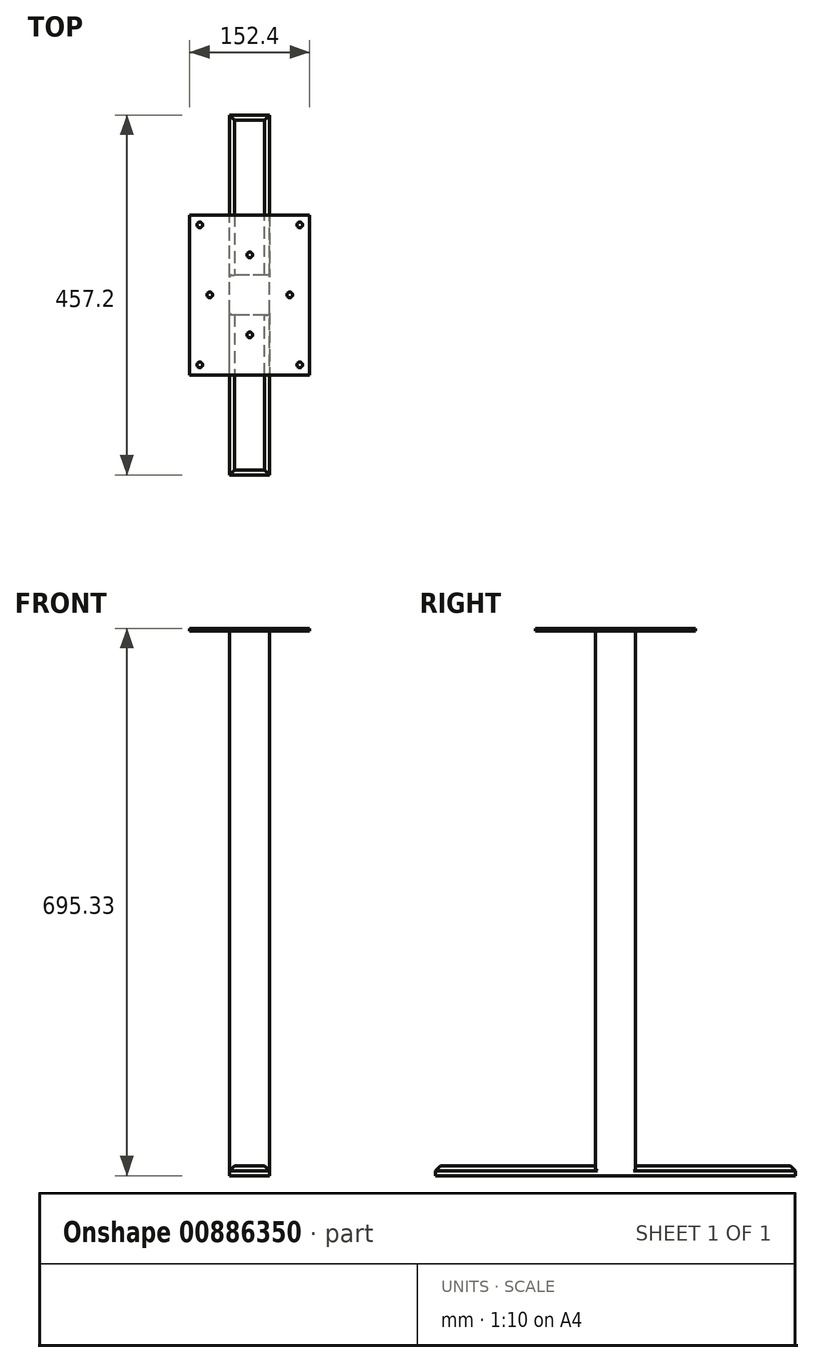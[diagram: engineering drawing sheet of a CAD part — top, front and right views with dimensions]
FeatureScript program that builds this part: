
annotation { "Feature Type Name" : "Feature", "Feature Type Description" : "" }
export const myFeature = defineFeature(function(context is Context, id is Id, definition is map)
    precondition{}
    {
        {
            var Q0;
            Q0=qCreatedBy(makeId("Top.planeOp"),FACE);
            var sketch = newSketch(context, id + "F0", { "sketchPlane" : qUnion([Q0])});
            skLineSegment(sketch, "E0.bottom", {"start": v(76.2, 101.6) * mm, "end": v(-76.2, 101.6) * mm});
            skLineSegment(sketch, "E0.top", {"start": v(76.2, -101.6) * mm, "end": v(-76.2, -101.6) * mm});
            skLineSegment(sketch, "E0.left", {"start": v(76.2, 101.6) * mm, "end": v(76.2, -101.6) * mm});
            skLineSegment(sketch, "E0.right", {"start": v(-76.2, 101.6) * mm, "end": v(-76.2, -101.6) * mm});
            skPoint(sketch, "E0.middle", {"position": v(0, 0) * mm});
            skSolve(sketch);
        }
        {
            var Q0;
            Q0 = qSketchRegion(id + "F0", true);
            extrude(context, id + "F1", {"entities" : qUnion([Q0]), "depth" : 3.17 * mm, "offsetDistance" : 25.4 * mm});
        }
        {
            var Q0;
            Q0=makeQuery(id+"F1.opExtrude","CAP_FACE",FACE,{"disambiguationData":[OSD([sQuery(id+"F0.wireOp",EDGE,"E0.bottom"),sQuery(id+"F0.wireOp",EDGE,"E0.top"),sQuery(id+"F0.wireOp",EDGE,"E0.left"),sQuery(id+"F0.wireOp",EDGE,"E0.right")])],"isStart":false});
            var sketch = newSketch(context, id + "F2", { "sketchPlane" : qUnion([Q0])});
            skLineSegment(sketch, "E1.bottom", {"start": v(63.5, 88.9) * mm, "end": v(-63.5, 88.9) * mm});
            skLineSegment(sketch, "E1.top", {"start": v(63.5, -88.9) * mm, "end": v(-63.5, -88.9) * mm});
            skLineSegment(sketch, "E1.left", {"start": v(63.5, 88.9) * mm, "end": v(63.5, -88.9) * mm});
            skLineSegment(sketch, "E1.right", {"start": v(-63.5, 88.9) * mm, "end": v(-63.5, -88.9) * mm});
            skPoint(sketch, "E1.middle", {"position": v(0, 0) * mm});
            skCircle(sketch, "E2", {"center": v(-63.5, 88.9) * mm, "radius": 3.57 * mm});
            skCircle(sketch, "E3", {"center": v(63.5, 88.9) * mm, "radius": 3.57 * mm});
            skCircle(sketch, "E4", {"center": v(63.5, -88.9) * mm, "radius": 3.57 * mm});
            skCircle(sketch, "E5", {"center": v(-63.5, -88.9) * mm, "radius": 3.57 * mm});
            skLineSegment(sketch, "E6.0", {"start": v(0, 50.8) * mm, "end": v(50.8, 0) * mm});
            skLineSegment(sketch, "E6.1", {"start": v(50.8, 0) * mm, "end": v(0, -50.8) * mm});
            skLineSegment(sketch, "E6.2", {"start": v(0, -50.8) * mm, "end": v(-50.8, 0) * mm});
            skLineSegment(sketch, "E6.3", {"start": v(-50.8, 0) * mm, "end": v(0, 50.8) * mm});
            skPoint(sketch, "E7", {"position": v(0, 50.8) * mm});
            skCircle(sketch, "E8", {"center": v(0, 50.8) * mm, "radius": 3.57 * mm});
            skCircle(sketch, "E9", {"center": v(-50.8, 0) * mm, "radius": 3.57 * mm});
            skCircle(sketch, "E10", {"center": v(50.8, 0) * mm, "radius": 3.57 * mm});
            skCircle(sketch, "E11", {"center": v(0, -50.8) * mm, "radius": 3.57 * mm});
            skSolve(sketch);
        }
        {
            var Q0;
            {var subQ0=sQuery(id+"F2.wireOp",EDGE,"E6.3");var subQ1=sQuery(id+"F2.wireOp",EDGE,"E6.0");var subQ2=makeQuery(id+"F2.imprint","INTERSECT",VERTEX,{"derivedFrom":[subQ1,subQ0]});Q0=makeQuery(id+"F2.imprint","IMPRINT",FACE,{"disambiguationData":[TD([[makeQuery(id+"F2.imprint","IMPRINT",EDGE,{"disambiguationData":[TD([[subQ2,-1.0]])],"derivedFrom":subQ1}),1.0]])]});}
            var Q1;
            {var subQ0=sQuery(id+"F2.wireOp",EDGE,"E6.3");var subQ1=sQuery(id+"F2.wireOp",EDGE,"E6.0");var subQ2=makeQuery(id+"F2.imprint","INTERSECT",VERTEX,{"derivedFrom":[subQ1,subQ0]});Q1=makeQuery(id+"F2.imprint","IMPRINT",FACE,{"disambiguationData":[TD([[makeQuery(id+"F2.imprint","IMPRINT",EDGE,{"disambiguationData":[TD([[subQ2,-1.0]])],"derivedFrom":subQ1}),-1.0]])]});}
            var Q2;
            {var subQ0=sQuery(id+"F2.wireOp",EDGE,"E6.3");var subQ1=sQuery(id+"F2.wireOp",EDGE,"E6.2");var subQ2=makeQuery(id+"F2.imprint","INTERSECT",VERTEX,{"derivedFrom":[subQ1,subQ0]});Q2=makeQuery(id+"F2.imprint","IMPRINT",FACE,{"disambiguationData":[TD([[makeQuery(id+"F2.imprint","IMPRINT",EDGE,{"disambiguationData":[TD([[subQ2,1.0]])],"derivedFrom":subQ1}),1.0]])]});}
            var Q3;
            {var subQ0=sQuery(id+"F2.wireOp",EDGE,"E6.3");var subQ1=sQuery(id+"F2.wireOp",EDGE,"E6.2");var subQ2=makeQuery(id+"F2.imprint","INTERSECT",VERTEX,{"derivedFrom":[subQ1,subQ0]});Q3=makeQuery(id+"F2.imprint","IMPRINT",FACE,{"disambiguationData":[TD([[makeQuery(id+"F2.imprint","IMPRINT",EDGE,{"disambiguationData":[TD([[subQ2,1.0]])],"derivedFrom":subQ1}),-1.0]])]});}
            var Q4;
            {var subQ0=sQuery(id+"F2.wireOp",EDGE,"E6.1");var subQ1=sQuery(id+"F2.wireOp",EDGE,"E6.0");var subQ2=makeQuery(id+"F2.imprint","INTERSECT",VERTEX,{"derivedFrom":[subQ1,subQ0]});Q4=makeQuery(id+"F2.imprint","IMPRINT",FACE,{"disambiguationData":[TD([[makeQuery(id+"F2.imprint","IMPRINT",EDGE,{"disambiguationData":[TD([[subQ2,1.0]])],"derivedFrom":subQ1}),-1.0]])]});}
            var Q5;
            {var subQ0=sQuery(id+"F2.wireOp",EDGE,"E6.1");var subQ1=sQuery(id+"F2.wireOp",EDGE,"E6.0");var subQ2=makeQuery(id+"F2.imprint","INTERSECT",VERTEX,{"derivedFrom":[subQ1,subQ0]});Q5=makeQuery(id+"F2.imprint","IMPRINT",FACE,{"disambiguationData":[TD([[makeQuery(id+"F2.imprint","IMPRINT",EDGE,{"disambiguationData":[TD([[subQ2,1.0]])],"derivedFrom":subQ1}),1.0]])]});}
            var Q6;
            {var subQ0=sQuery(id+"F2.wireOp",EDGE,"E6.2");var subQ1=sQuery(id+"F2.wireOp",EDGE,"E6.1");var subQ2=makeQuery(id+"F2.imprint","INTERSECT",VERTEX,{"derivedFrom":[subQ1,subQ0]});Q6=makeQuery(id+"F2.imprint","IMPRINT",FACE,{"disambiguationData":[TD([[makeQuery(id+"F2.imprint","IMPRINT",EDGE,{"disambiguationData":[TD([[subQ2,1.0]])],"derivedFrom":subQ1}),-1.0]])]});}
            var Q7;
            {var subQ0=sQuery(id+"F2.wireOp",EDGE,"E6.2");var subQ1=sQuery(id+"F2.wireOp",EDGE,"E6.1");var subQ2=makeQuery(id+"F2.imprint","INTERSECT",VERTEX,{"derivedFrom":[subQ1,subQ0]});Q7=makeQuery(id+"F2.imprint","IMPRINT",FACE,{"disambiguationData":[TD([[makeQuery(id+"F2.imprint","IMPRINT",EDGE,{"disambiguationData":[TD([[subQ2,1.0]])],"derivedFrom":subQ1}),1.0]])]});}
            var Q8;
            {var subQ0=sQuery(id+"F2.wireOp",EDGE,"E1.right");var subQ1=sQuery(id+"F2.wireOp",EDGE,"E1.top");var subQ2=makeQuery(id+"F2.imprint","INTERSECT",VERTEX,{"derivedFrom":[subQ1,subQ0]});Q8=makeQuery(id+"F2.imprint","IMPRINT",FACE,{"disambiguationData":[TD([[makeQuery(id+"F2.imprint","IMPRINT",EDGE,{"disambiguationData":[TD([[subQ2,1.0]])],"derivedFrom":subQ1}),-1.0]])]});}
            var Q9;
            {var subQ0=sQuery(id+"F2.wireOp",EDGE,"E1.right");var subQ1=sQuery(id+"F2.wireOp",EDGE,"E1.top");var subQ2=makeQuery(id+"F2.imprint","INTERSECT",VERTEX,{"derivedFrom":[subQ1,subQ0]});Q9=makeQuery(id+"F2.imprint","IMPRINT",FACE,{"disambiguationData":[TD([[makeQuery(id+"F2.imprint","IMPRINT",EDGE,{"disambiguationData":[TD([[subQ2,1.0]])],"derivedFrom":subQ1}),1.0]])]});}
            var Q10;
            {var subQ0=sQuery(id+"F2.wireOp",EDGE,"E1.left");var subQ1=sQuery(id+"F2.wireOp",EDGE,"E1.top");var subQ2=makeQuery(id+"F2.imprint","INTERSECT",VERTEX,{"derivedFrom":[subQ1,subQ0]});Q10=makeQuery(id+"F2.imprint","IMPRINT",FACE,{"disambiguationData":[TD([[makeQuery(id+"F2.imprint","IMPRINT",EDGE,{"disambiguationData":[TD([[subQ2,-1.0]])],"derivedFrom":subQ1}),-1.0]])]});}
            var Q11;
            {var subQ0=sQuery(id+"F2.wireOp",EDGE,"E1.left");var subQ1=sQuery(id+"F2.wireOp",EDGE,"E1.top");var subQ2=makeQuery(id+"F2.imprint","INTERSECT",VERTEX,{"derivedFrom":[subQ1,subQ0]});Q11=makeQuery(id+"F2.imprint","IMPRINT",FACE,{"disambiguationData":[TD([[makeQuery(id+"F2.imprint","IMPRINT",EDGE,{"disambiguationData":[TD([[subQ2,-1.0]])],"derivedFrom":subQ1}),1.0]])]});}
            var Q12;
            {var subQ0=sQuery(id+"F2.wireOp",EDGE,"E1.left");var subQ1=sQuery(id+"F2.wireOp",EDGE,"E1.bottom");var subQ2=makeQuery(id+"F2.imprint","INTERSECT",VERTEX,{"derivedFrom":[subQ1,subQ0]});Q12=makeQuery(id+"F2.imprint","IMPRINT",FACE,{"disambiguationData":[TD([[makeQuery(id+"F2.imprint","IMPRINT",EDGE,{"disambiguationData":[TD([[subQ2,-1.0]])],"derivedFrom":subQ1}),-1.0]])]});}
            var Q13;
            {var subQ0=sQuery(id+"F2.wireOp",EDGE,"E1.left");var subQ1=sQuery(id+"F2.wireOp",EDGE,"E1.bottom");var subQ2=makeQuery(id+"F2.imprint","INTERSECT",VERTEX,{"derivedFrom":[subQ1,subQ0]});Q13=makeQuery(id+"F2.imprint","IMPRINT",FACE,{"disambiguationData":[TD([[makeQuery(id+"F2.imprint","IMPRINT",EDGE,{"disambiguationData":[TD([[subQ2,-1.0]])],"derivedFrom":subQ1}),1.0]])]});}
            var Q14;
            {var subQ0=sQuery(id+"F2.wireOp",EDGE,"E1.right");var subQ1=sQuery(id+"F2.wireOp",EDGE,"E1.bottom");var subQ2=makeQuery(id+"F2.imprint","INTERSECT",VERTEX,{"derivedFrom":[subQ1,subQ0]});Q14=makeQuery(id+"F2.imprint","IMPRINT",FACE,{"disambiguationData":[TD([[makeQuery(id+"F2.imprint","IMPRINT",EDGE,{"disambiguationData":[TD([[subQ2,1.0]])],"derivedFrom":subQ1}),-1.0]])]});}
            var Q15;
            {var subQ0=sQuery(id+"F2.wireOp",EDGE,"E1.right");var subQ1=sQuery(id+"F2.wireOp",EDGE,"E1.bottom");var subQ2=makeQuery(id+"F2.imprint","INTERSECT",VERTEX,{"derivedFrom":[subQ1,subQ0]});Q15=makeQuery(id+"F2.imprint","IMPRINT",FACE,{"disambiguationData":[TD([[makeQuery(id+"F2.imprint","IMPRINT",EDGE,{"disambiguationData":[TD([[subQ2,1.0]])],"derivedFrom":subQ1}),1.0]])]});}
            extrude(context, id + "F3", {"entities" : qUnion([Q0, Q1, Q2, Q3, Q4, Q5, Q6, Q7, Q8, Q9, Q10, Q11, Q12, Q13, Q14, Q15]), "operationType" : NewBodyOperationType.REMOVE, "oppositeDirection" : true, "depth" : 25.4 * mm, "offsetDistance" : 25.4 * mm});
        }
        {
            var Q0;
            Q0=makeQuery(id+"F1.opExtrude","CAP_FACE",FACE,{"disambiguationData":[OSD([sQuery(id+"F0.wireOp",EDGE,"E0.bottom"),sQuery(id+"F0.wireOp",EDGE,"E0.top"),sQuery(id+"F0.wireOp",EDGE,"E0.left"),sQuery(id+"F0.wireOp",EDGE,"E0.right")])],"isStart":true});
            var sketch = newSketch(context, id + "F4", { "sketchPlane" : qUnion([Q0])});
            skLineSegment(sketch, "E12.bottom", {"start": v(25.4, 25.4) * mm, "end": v(-25.4, 25.4) * mm});
            skLineSegment(sketch, "E12.top", {"start": v(25.4, -25.4) * mm, "end": v(-25.4, -25.4) * mm});
            skLineSegment(sketch, "E12.left", {"start": v(25.4, 25.4) * mm, "end": v(25.4, -25.4) * mm});
            skLineSegment(sketch, "E12.right", {"start": v(-25.4, 25.4) * mm, "end": v(-25.4, -25.4) * mm});
            skPoint(sketch, "E12.middle", {"position": v(0, 0) * mm});
            skSolve(sketch);
        }
        {
            var Q0;
            Q0=makeQuery(id+"F4.imprint","IMPRINT",FACE,{"disambiguationData":[TD([[makeQuery(id+"F4.imprint","IMPRINT",EDGE,{"derivedFrom":sQuery(id+"F4.wireOp",EDGE,"E12.bottom")}),1.0]])]});
            extrude(context, id + "F5", {"entities" : qUnion([Q0]), "operationType" : NewBodyOperationType.ADD, "depth" : 679.45 * mm, "offsetDistance" : 25.4 * mm});
        }
        {
            var Q0;
            Q0=makeQuery(id+"F5.opExtrude","SWEPT_EDGE",EDGE,{"disambiguationData":[OSD([sQuery(id+"F4.wireOp",EDGE,"E12.bottom"),sQuery(id+"F4.wireOp",EDGE,"E12.right")])]});
            var Q1;
            Q1=makeQuery(id+"F5.opExtrude","SWEPT_EDGE",EDGE,{"disambiguationData":[OSD([sQuery(id+"F4.wireOp",EDGE,"E12.bottom"),sQuery(id+"F4.wireOp",EDGE,"E12.left")])]});
            var Q2;
            Q2=makeQuery(id+"F5.opExtrude","SWEPT_EDGE",EDGE,{"disambiguationData":[OSD([sQuery(id+"F4.wireOp",EDGE,"E12.top"),sQuery(id+"F4.wireOp",EDGE,"E12.left")])]});
            var Q3;
            Q3=makeQuery(id+"F5.opExtrude","SWEPT_EDGE",EDGE,{"disambiguationData":[OSD([sQuery(id+"F4.wireOp",EDGE,"E12.top"),sQuery(id+"F4.wireOp",EDGE,"E12.right")])]});
            fillet(context, id + "F6", {"entities" : qUnion([Q0, Q1, Q2, Q3]), "radius" : 2.54 * mm, "tangentPropagation" : true, "allowEdgeOverflow" : false});
        }
        {
            var Q0;
            Q0=makeQuery(id+"F5.opExtrude","CAP_FACE",FACE,{"disambiguationData":[OSD([sQuery(id+"F4.wireOp",EDGE,"E12.bottom"),sQuery(id+"F4.wireOp",EDGE,"E12.top"),sQuery(id+"F4.wireOp",EDGE,"E12.left"),sQuery(id+"F4.wireOp",EDGE,"E12.right")])],"isStart":false});
            var sketch = newSketch(context, id + "F7", { "sketchPlane" : qUnion([Q0])});
            skLineSegment(sketch, "E13.bottom", {"start": v(25.4, 228.6) * mm, "end": v(-25.4, 228.6) * mm});
            skLineSegment(sketch, "E13.top", {"start": v(25.4, -228.6) * mm, "end": v(-25.4, -228.6) * mm});
            skLineSegment(sketch, "E13.left", {"start": v(25.4, 228.6) * mm, "end": v(25.4, -228.6) * mm});
            skLineSegment(sketch, "E13.right", {"start": v(-25.4, 228.6) * mm, "end": v(-25.4, -228.6) * mm});
            skPoint(sketch, "E13.middle", {"position": v(0, 0) * mm});
            skSolve(sketch);
        }
        {
            var Q0;
            {var subQ6=sQuery(id+"F7.wireOp",EDGE,"E13.bottom");Q0=makeQuery(id+"F7.imprint","IMPRINT",FACE,{"disambiguationData":[TD([[makeQuery(id+"F7.imprint","IMPRINT",EDGE,{"derivedFrom":subQ6}),1.0]])]});}
            var Q1;
            {var subQ6=sQuery(id+"F7.wireOp",EDGE,"E13.top");Q1=makeQuery(id+"F7.imprint","IMPRINT",FACE,{"disambiguationData":[TD([[makeQuery(id+"F7.imprint","IMPRINT",EDGE,{"derivedFrom":subQ6}),-1.0]])]});}
            var Q2;
            {var subQ3=sQuery(id+"F4.wireOp",EDGE,"E12.bottom");Q2=makeQuery(id+"F7.imprint","IMPRINT",FACE,{"disambiguationData":[TD([[makeQuery(id+"F7.imprint","IMPRINT",EDGE,{"derivedFrom":makeQuery(id+"F5.opExtrude","CAP_EDGE",EDGE,{"disambiguationData":[OSD([subQ3])],"isStart":false})}),1.0]])]});}
            extrude(context, id + "F8", {"entities" : qUnion([Q0, Q1, Q2]), "operationType" : NewBodyOperationType.ADD, "depth" : 12.7 * mm, "offsetDistance" : 25.4 * mm});
        }
        {
            var Q0;
            Q0=makeQuery(id+"F8.opExtrude","CAP_EDGE",EDGE,{"disambiguationData":[OSD([sQuery(id+"F7.wireOp",EDGE,"E13.bottom")])],"isStart":true});
            var Q1;
            Q1=makeQuery(id+"F8.opExtrude","CAP_EDGE",EDGE,{"disambiguationData":[OSD([sQuery(id+"F7.wireOp",EDGE,"E13.top")])],"isStart":true});
            chamfer(context, id + "F9", {"entities" : qUnion([Q0, Q1]), "chamferType" : ChamferType.OFFSET_ANGLE, "width" : 6.35 * mm, "oppositeDirection" : false, "angle" : 45 * degree, "tangentPropagation" : true});
        }
        {
            var Q0;
            {var subQ0=sQuery(id+"F7.wireOp",EDGE,"E13.left");var subQ1=sQuery(id+"F7.wireOp",EDGE,"E13.bottom");Q0=makeQuery(id+"F8.boolean.opBoolean","SPLIT",EDGE,{"disambiguationData":[TD([makeQuery(id+"F8.opExtrude","SWEPT_FACE",FACE,{"disambiguationData":[OSD([subQ1])]})])],"derivedFrom":makeQuery(id+"F8.opExtrude","CAP_EDGE",EDGE,{"disambiguationData":[OSD([subQ0])],"isStart":true})});}
            var Q1;
            {var subQ0=sQuery(id+"F7.wireOp",EDGE,"E13.right");var subQ1=sQuery(id+"F7.wireOp",EDGE,"E13.bottom");Q1=makeQuery(id+"F8.boolean.opBoolean","SPLIT",EDGE,{"disambiguationData":[TD([makeQuery(id+"F8.opExtrude","SWEPT_FACE",FACE,{"disambiguationData":[OSD([subQ1])]})])],"derivedFrom":makeQuery(id+"F8.opExtrude","CAP_EDGE",EDGE,{"disambiguationData":[OSD([subQ0])],"isStart":true})});}
            var Q2;
            {var subQ0=sQuery(id+"F7.wireOp",EDGE,"E13.top");var subQ1=sQuery(id+"F7.wireOp",EDGE,"E13.right");Q2=makeQuery(id+"F8.boolean.opBoolean","SPLIT",EDGE,{"disambiguationData":[TD([makeQuery(id+"F8.opExtrude","SWEPT_FACE",FACE,{"disambiguationData":[OSD([subQ0])]})])],"derivedFrom":makeQuery(id+"F8.opExtrude","CAP_EDGE",EDGE,{"disambiguationData":[OSD([subQ1])],"isStart":true})});}
            var Q3;
            {var subQ0=sQuery(id+"F7.wireOp",EDGE,"E13.top");var subQ1=sQuery(id+"F7.wireOp",EDGE,"E13.left");Q3=makeQuery(id+"F8.boolean.opBoolean","SPLIT",EDGE,{"disambiguationData":[TD([makeQuery(id+"F8.opExtrude","SWEPT_FACE",FACE,{"disambiguationData":[OSD([subQ0])]})])],"derivedFrom":makeQuery(id+"F8.opExtrude","CAP_EDGE",EDGE,{"disambiguationData":[OSD([subQ1])],"isStart":true})});}
            chamfer(context, id + "F10", {"entities" : qUnion([Q0, Q1, Q2, Q3]), "width" : 6.35 * mm, "tangentPropagation" : true});
        }
    });
